# Revit family: Backflow_Preventer-RP-Zurn_Wilkins-Model_475DABG(8-10_Inch)
name_source: partatom
category: Pipe Accessories
units: mm (PartAtom-declared; Revit-internal decimal feet)

## family parameters
Always vertical = Yes
Cut with Voids When Loaded = No
OmniClass Number = 23.65.55.14.21
OmniClass Title = Non-Return Valves for Liquid Services
Part Type = Valve - Breaks Into
Round Connector Dimension = Use Radius
Shared = No
Work Plane-Based = No

## types (2) — shared parameters
Assembly Code = D2020300
Bend Radius = 1"
Bend Radius Outside = 2"
DA Front = 5"
DA Height = 18"
DIM A - VALVE INLET CENTER TO OUTLET CENTER = 29"
DIM D Valve Center to DA End = 13"
Default Elevation = 0"
Description = Reduced Pressure Detector Assembly
Flow Rate (GPM) = 0 GPM
Hydrostatic Test Pressure = 350.00 psi
Length = 29"
MR body flange dia-1 = 12 1/2"
MR body flange dia-2 = 14 1/2"
Main Material = Paint - Zurn - Ductile Iron - Blue
Manufacturer = Zurn Water, LLC
Manufacturer Brand = Zurn Wilkins
Max Working Water Pressure = 175.00 psi
Max Working Water Temperature = 140 °F
Model = 475DABG
Modified Date = 07/22/2025
Overall Length = 29"
Pipe Size = 1"
Product Documentation Link = https://files.zurn.com
Product Installation Sheet URL = https://files.zurn.com
Product Page URL = https://www.zurn.com
Product data URL = https://www.bimobject.com
Repair Parts URL = https://files.zurn.com
URL = https://www.zurn.com
VALVE CENTER TO END = 10"

## per-type parameters (varying)
| type | Bypass | DIM B - OVERALL HEIGHT OF THE VALVE | DIM C - VALVE CENTER TO GATE STEM END | Gate valve | Height | Main Body DA | Nominal Diameter | Nominal Radius | Overall Height | Pressure Loss at Rated Flow | Product Weight (lbs) | Rated Flow |
| 8-475DABG (8" 475DA Butterfly Grooved) | Bypass 475DA(8-10_inch) : 8" | 42 1/2" | 12" | Shut_Off_Valve-Butterfly-Zurn_Wilkins-Model_49G_Grooved-(8-10_inch) : 8-49G (8" 49G) | 46" | Main Body 475OSY : 8" | 8" | 4" | 46" | 15.00 psi | 565 | 1600 GPM |
| 10-475DABG (10" 475DA Butterfly Grooved) | Bypass 475DA(8-10_inch) : 10" | 44 1/2" | 13" | Shut_Off_Valve-Butterfly-Zurn_Wilkins-Model_49G_Grooved-(8-10_inch) : 10-49G (10" 49G) | 47 1/2" | Main Body 475OSY : 10" | 10" | 5" | 47 1/2" | 14.60 psi | 655 | 2300 GPM |

## geometry (parser evidence)
native form markers: Sweep x11
no freeform markers — native parametric forms only
